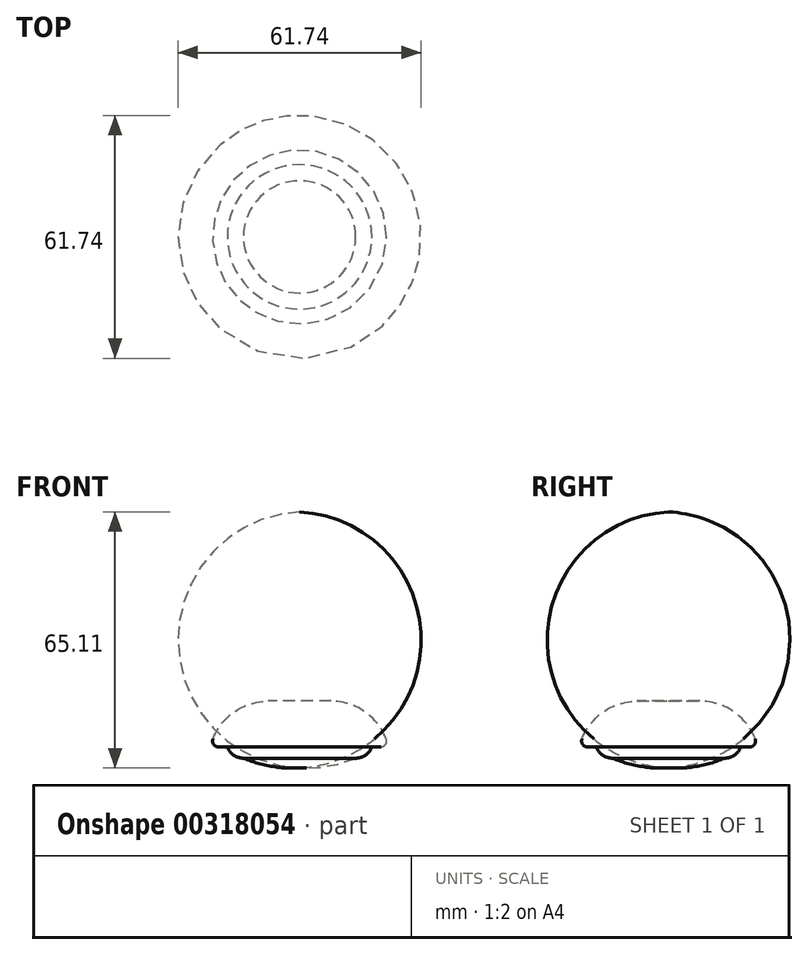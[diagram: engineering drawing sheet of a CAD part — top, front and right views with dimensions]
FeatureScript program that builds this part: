
annotation { "Feature Type Name" : "Feature", "Feature Type Description" : "" }
export const myFeature = defineFeature(function(context is Context, id is Id, definition is map)
    precondition{}
    {
        {
            var Q0;
            Q0=qCreatedBy(makeId("Front.planeOp"),FACE);
            var sketch = newSketch(context, id + "F0", { "sketchPlane" : qUnion([Q0])});
            skLineSegment(sketch, "E0", {"start": v(0, 0) * mm, "end": v(8, 0) * mm});
            skArc(sketch, "E1", {"start": v(22, -9.61) * mm, "mid": v(16.5, -2.64) * mm, "end": v(8, 0) * mm});
            skArc(sketch, "E2", {"start": v(22, -9.61) * mm, "mid": v(21.84, -10.98) * mm, "end": v(20.62, -11.63) * mm});
            skLineSegment(sketch, "E3", {"start": v(20.62, -11.63) * mm, "end": v(0, -11.63) * mm});
            skLineSegment(sketch, "E4", {"start": v(0, -14.5) * mm, "end": v(14.26, -14.5) * mm});
            skArc(sketch, "E5", {"start": v(14.26, -14.5) * mm, "mid": v(16.76, -13.71) * mm, "end": v(18.35, -11.63) * mm});
            skArc(sketch, "E6", {"start": v(0, -16.97) * mm, "mid": v(7.27, -16.54) * mm, "end": v(14.26, -14.5) * mm});
            skLineSegment(sketch, "E7", {"start": v(0, 0) * mm, "end": v(0, -16.97) * mm});
            skSolve(sketch);
        }
        {
            var Q0;
            Q0 = qSketchRegion(id + "F0", true);
            var Q1;
            Q1=sQuery(id+"F0.wireOp",EDGE,"E7");
            revolve(context, id + "F1", {"entities" : qUnion([Q0]), "axis" : qUnion([Q1]), "revolveType" : RevolveType.FULL});
        }
        {
            var Q0;
            Q0 = qSketchRegion(id + "F0", true);
            var Q1;
            Q1=sQuery(id+"F0.wireOp",EDGE,"E7");
            revolve(context, id + "F2", {"entities" : qUnion([Q0]), "axis" : qUnion([Q1]), "revolveType" : RevolveType.FULL});
        }
    });
